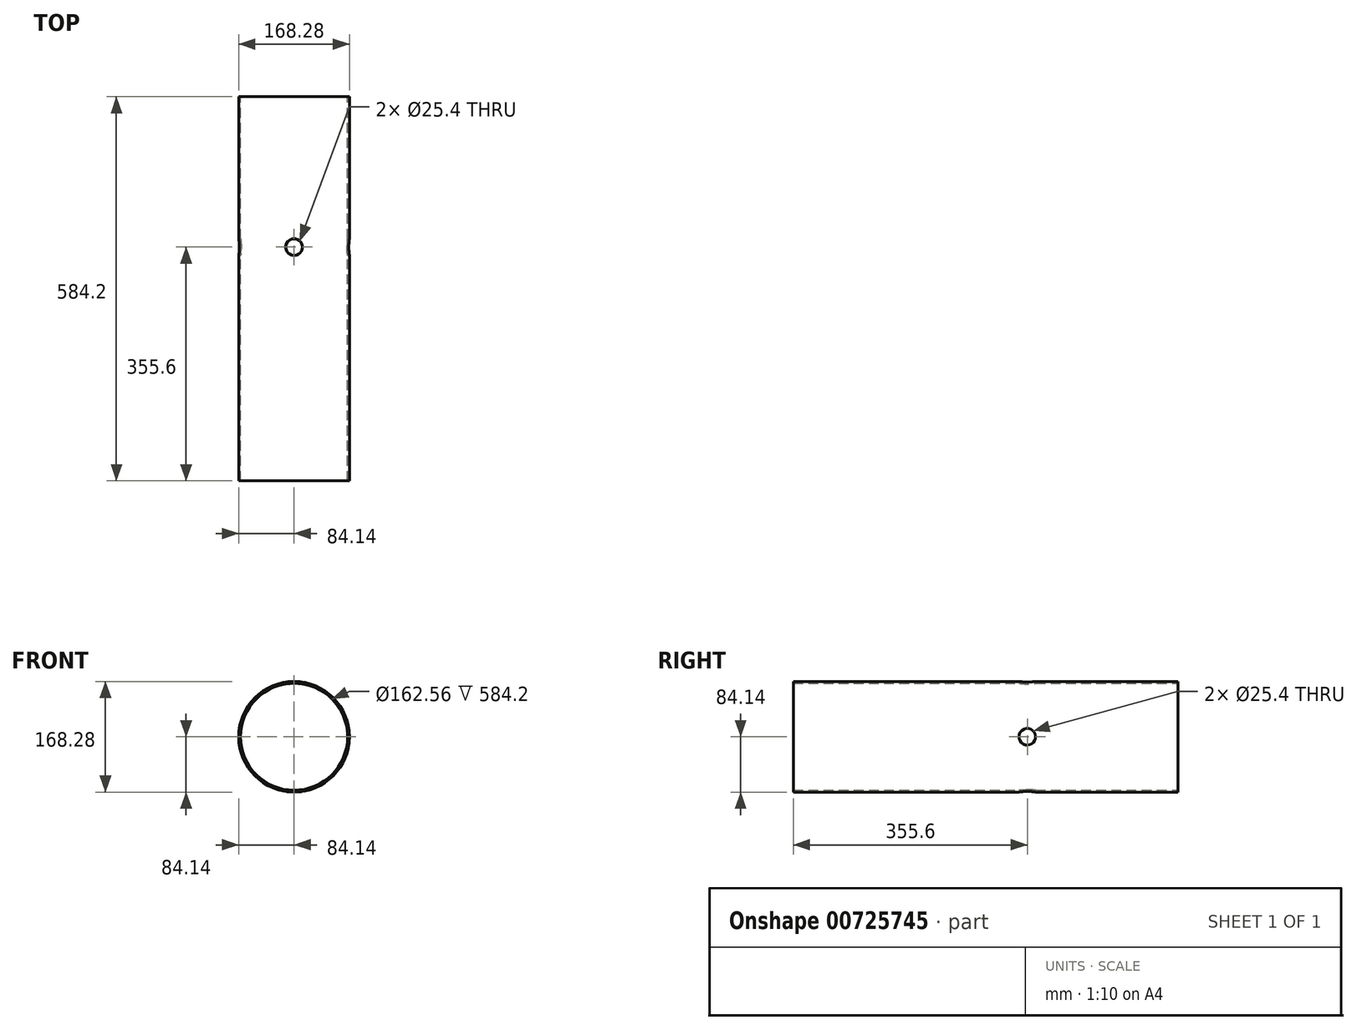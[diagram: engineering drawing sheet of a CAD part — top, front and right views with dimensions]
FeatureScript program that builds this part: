
annotation { "Feature Type Name" : "Feature", "Feature Type Description" : "" }
export const myFeature = defineFeature(function(context is Context, id is Id, definition is map)
    precondition{}
    {
        {
            var Q0;
            Q0=qCreatedBy(makeId("Front.planeOp"),FACE);
            var sketch = newSketch(context, id + "F0", { "sketchPlane" : qUnion([Q0])});
            skCircle(sketch, "E0", {"center": v(0, 0) * mm, "radius": 81.28 * mm});
            skCircle(sketch, "E1", {"center": v(0, 0) * mm, "radius": 84.14 * mm});
            skSolve(sketch);
        }
        {
            var Q0;
            Q0=makeQuery(id+"F0.imprint","IMPRINT",FACE,{"disambiguationData":[TD([[makeQuery(id+"F0.imprint","IMPRINT",EDGE,{"derivedFrom":sQuery(id+"F0.wireOp",EDGE,"E0")}),-1.0]])]});
            extrude(context, id + "F1", {"entities" : qUnion([Q0]), "depth" : 457.2 * mm, "offsetDistance" : 25.4 * mm});
        }
        {
            var Q0;
            Q0=qCreatedBy(makeId("Right.planeOp"),FACE);
            var sketch = newSketch(context, id + "F2", { "sketchPlane" : qUnion([Q0])});
            skCircle(sketch, "E2", {"center": v(-228.6, 0) * mm, "radius": 12.7 * mm});
            skSolve(sketch);
        }
        {
            var Q0;
            Q0 = qSketchRegion(id + "F2", true);
            extrude(context, id + "F3", {"entities" : qUnion([Q0]), "operationType" : NewBodyOperationType.REMOVE, "endBound" : BoundingType.SYMMETRIC, "oppositeDirection" : true, "depth" : 254 * mm, "offsetDistance" : 25.4 * mm});
        }
        {
            var Q0;
            Q0=qCreatedBy(makeId("Top.planeOp"),FACE);
            var sketch = newSketch(context, id + "F4", { "sketchPlane" : qUnion([Q0])});
            skCircle(sketch, "E3", {"center": v(0, -228.6) * mm, "radius": 12.7 * mm});
            skSolve(sketch);
        }
        {
            var Q0;
            Q0 = qSketchRegion(id + "F4", true);
            extrude(context, id + "F5", {"entities" : qUnion([Q0]), "operationType" : NewBodyOperationType.REMOVE, "endBound" : BoundingType.SYMMETRIC, "depth" : 254 * mm, "offsetDistance" : 25.4 * mm});
        }
        {
            var Q0;
            Q0=makeQuery(id+"F1.opExtrude","CAP_FACE",FACE,{"disambiguationData":[OSD([sQuery(id+"F0.wireOp",EDGE,"E0"),sQuery(id+"F0.wireOp",EDGE,"E1")])],"isStart":false});
            var sketch = newSketch(context, id + "F6", { "sketchPlane" : qUnion([Q0])});
            skCircle(sketch, "E4", {"center": v(0, 0) * mm, "radius": 81.28 * mm});
            skCircle(sketch, "E5", {"center": v(0, 0) * mm, "radius": 84.14 * mm});
            skSolve(sketch);
        }
        {
            var Q0;
            Q0 = qSketchRegion(id + "F6", true);
            extrude(context, id + "F7", {"entities" : qUnion([Q0]), "operationType" : NewBodyOperationType.ADD, "depth" : 127 * mm, "offsetDistance" : 25.4 * mm});
        }
    });
